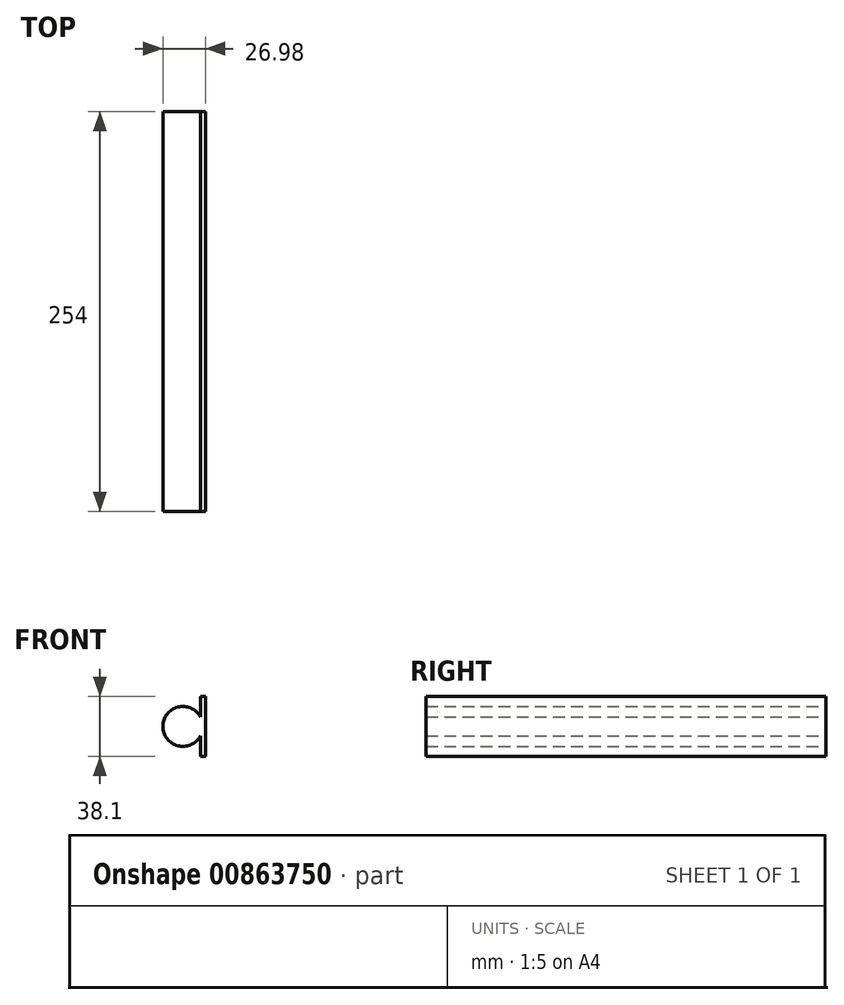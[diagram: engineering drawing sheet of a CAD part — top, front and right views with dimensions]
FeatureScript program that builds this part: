
annotation { "Feature Type Name" : "Feature", "Feature Type Description" : "" }
export const myFeature = defineFeature(function(context is Context, id is Id, definition is map)
    precondition{}
    {
        {
            var Q0;
            Q0=qCreatedBy(makeId("Front.planeOp"),FACE);
            var sketch = newSketch(context, id + "F0", { "sketchPlane" : qUnion([Q0])});
            skArc(sketch, "E0", {"start": v(11.1, 6.15) * mm, "mid": v(-12.7, 0) * mm, "end": v(11.1, -6.15) * mm});
            skLineSegment(sketch, "E1.bottom", {"start": v(14.28, -19.05) * mm, "end": v(11.1, -19.05) * mm});
            skLineSegment(sketch, "E1.top", {"start": v(14.28, 19.05) * mm, "end": v(11.1, 19.05) * mm});
            skLineSegment(sketch, "E1.left", {"start": v(14.28, -19.05) * mm, "end": v(14.28, 19.05) * mm});
            skLineSegment(sketch, "E1.right", {"start": v(11.1, -19.05) * mm, "end": v(11.1, -6.15) * mm});
            skPoint(sketch, "E1.middle", {"position": v(12.7, 0) * mm});
            skLineSegment(sketch, "E2.trimOffspring", {"start": v(11.1, 6.15) * mm, "end": v(11.1, 19.05) * mm});
            skSolve(sketch);
        }
        {
            var Q0;
            Q0=makeQuery(id+"F0.imprint","IMPRINT",FACE,{"disambiguationData":[TD([[makeQuery(id+"F0.imprint","IMPRINT",EDGE,{"derivedFrom":sQuery(id+"F0.wireOp",EDGE,"E0")}),1.0]])]});
            extrude(context, id + "F1", {"entities" : qUnion([Q0]), "endBound" : BoundingType.SYMMETRIC, "depth" : 254 * mm, "offsetDistance" : 25.4 * mm});
        }
    });
